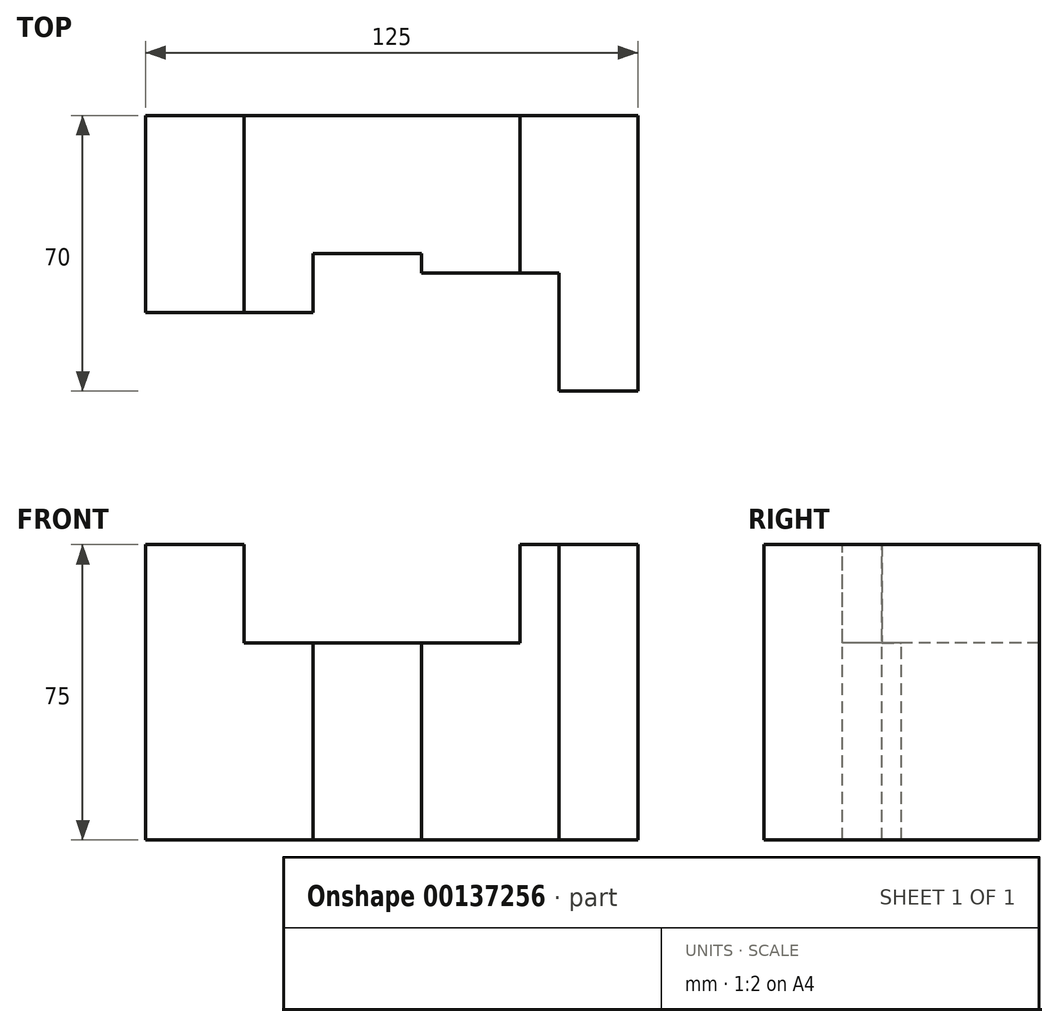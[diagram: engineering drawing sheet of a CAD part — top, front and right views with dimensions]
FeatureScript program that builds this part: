
annotation { "Feature Type Name" : "Feature", "Feature Type Description" : "" }
export const myFeature = defineFeature(function(context is Context, id is Id, definition is map)
    precondition{}
    {
        {
            var Q0;
            Q0=qCreatedBy(makeId("Front.planeOp"),FACE);
            var sketch = newSketch(context, id + "F0", { "sketchPlane" : qUnion([Q0])});
            skLineSegment(sketch, "E0", {"start": v(0, 0) * mm, "end": v(125, 0) * mm});
            skLineSegment(sketch, "E1", {"start": v(125, 0) * mm, "end": v(125, 75) * mm});
            skLineSegment(sketch, "E2", {"start": v(125, 75) * mm, "end": v(0, 75) * mm});
            skLineSegment(sketch, "E3", {"start": v(0, 75) * mm, "end": v(0, 0) * mm});
            skSolve(sketch);
        }
        {
            var Q0;
            Q0 = qSketchRegion(id + "F0", true);
            extrude(context, id + "F1", {"entities" : qUnion([Q0]), "oppositeDirection" : true, "depth" : 70 * mm});
        }
        {
            var Q0;
            Q0=makeQuery(id+"F1.opExtrude","CAP_FACE",FACE,{"disambiguationData":[OSD([sQuery(id+"F0.wireOp",EDGE,"E0"),sQuery(id+"F0.wireOp",EDGE,"E1"),sQuery(id+"F0.wireOp",EDGE,"E2"),sQuery(id+"F0.wireOp",EDGE,"E3")])],"isStart":true});
            var sketch = newSketch(context, id + "F2", { "sketchPlane" : qUnion([Q0])});
            skLineSegment(sketch, "E4", {"start": v(25, 75) * mm, "end": v(25, 50) * mm});
            skLineSegment(sketch, "E5", {"start": v(25, 50) * mm, "end": v(95, 50) * mm});
            skLineSegment(sketch, "E6", {"start": v(95, 50) * mm, "end": v(95, 75) * mm});
            skLineSegment(sketch, "E7", {"start": v(95, 75) * mm, "end": v(25, 75) * mm});
            skSolve(sketch);
        }
        {
            var Q0;
            Q0 = qSketchRegion(id + "F2", true);
            extrude(context, id + "F3", {"entities" : qUnion([Q0]), "operationType" : NewBodyOperationType.REMOVE, "endBound" : BoundingType.THROUGH_ALL, "oppositeDirection" : true, "depth" : 25 * mm});
        }
        {
            var Q0;
            {var subQ0=sQuery(id+"F0.wireOp",EDGE,"E3");var subQ1=sQuery(id+"F0.wireOp",EDGE,"E2");Q0=makeQuery(id+"F3.boolean.opBoolean","SPLIT",FACE,{"disambiguationData":[TD([makeQuery(id+"F1.opExtrude","SWEPT_FACE",FACE,{"disambiguationData":[OSD([subQ0])]})])],"derivedFrom":makeQuery(id+"F1.opExtrude","SWEPT_FACE",FACE,{"disambiguationData":[OSD([subQ1])]})});}
            var sketch = newSketch(context, id + "F4", { "sketchPlane" : qUnion([Q0])});
            skLineSegment(sketch, "E8", {"start": v(0, 20) * mm, "end": v(42.5, 20) * mm});
            skLineSegment(sketch, "E9", {"start": v(42.5, 20) * mm, "end": v(42.5, 35) * mm});
            skLineSegment(sketch, "E10", {"start": v(42.5, 35) * mm, "end": v(70, 35) * mm});
            skLineSegment(sketch, "E11", {"start": v(70, 35) * mm, "end": v(70, 30) * mm});
            skLineSegment(sketch, "E12", {"start": v(70, 30) * mm, "end": v(105, 30) * mm});
            skLineSegment(sketch, "E13", {"start": v(105, 30) * mm, "end": v(105, 0) * mm});
            skLineSegment(sketch, "E14", {"start": v(105, 0) * mm, "end": v(0, 0) * mm});
            skLineSegment(sketch, "E15", {"start": v(0, 0) * mm, "end": v(0, 20) * mm});
            skSolve(sketch);
        }
        {
            var Q0;
            Q0 = qSketchRegion(id + "F4", true);
            extrude(context, id + "F5", {"entities" : qUnion([Q0]), "operationType" : NewBodyOperationType.REMOVE, "endBound" : BoundingType.THROUGH_ALL, "oppositeDirection" : true, "depth" : 25 * mm});
        }
    });
